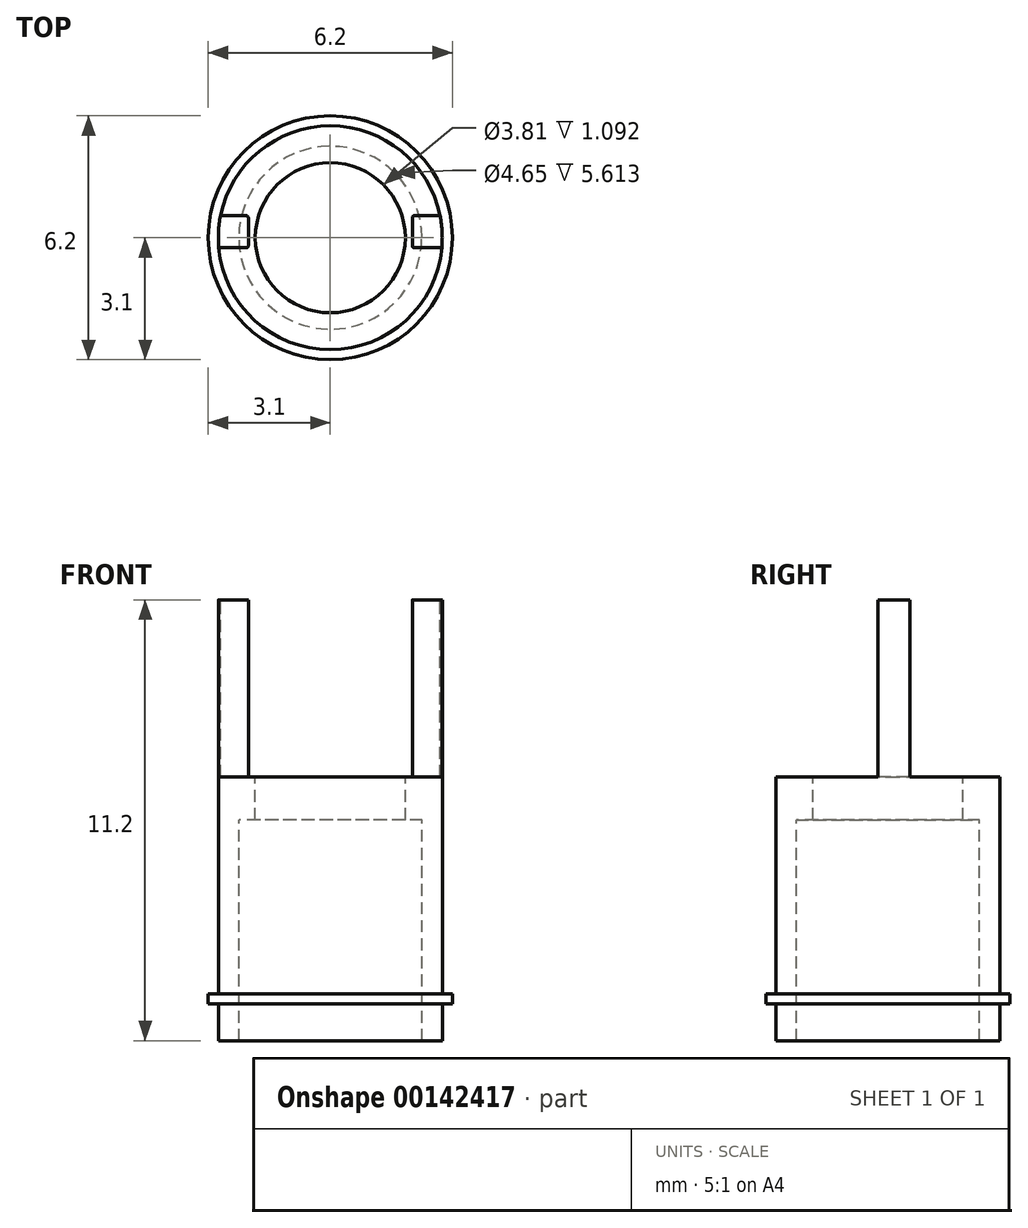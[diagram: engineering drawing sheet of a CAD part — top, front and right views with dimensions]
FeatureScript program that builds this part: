
annotation { "Feature Type Name" : "Feature", "Feature Type Description" : "" }
export const myFeature = defineFeature(function(context is Context, id is Id, definition is map)
    precondition{}
    {
        {
            var Q0;
            Q0=qCreatedBy(makeId("Right.planeOp"),FACE);
            var sketch = newSketch(context, id + "F0", { "sketchPlane" : qUnion([Q0])});
            skLineSegment(sketch, "E0", {"start": v(0, 0) * mm, "end": v(0, -11.2) * mm, "construction": true});
            skLineSegment(sketch, "E1", {"start": v(1.9, 0) * mm, "end": v(2.84, 0) * mm});
            skLineSegment(sketch, "E2", {"start": v(2.84, 0) * mm, "end": v(2.84, -10) * mm});
            skLineSegment(sketch, "E3", {"start": v(2.84, -10) * mm, "end": v(3.1, -10) * mm});
            skLineSegment(sketch, "E4", {"start": v(3.1, -10) * mm, "end": v(3.1, -10.26) * mm});
            skLineSegment(sketch, "E5", {"start": v(3.1, -10.26) * mm, "end": v(2.84, -10.26) * mm});
            skLineSegment(sketch, "E6", {"start": v(2.84, -10.26) * mm, "end": v(2.84, -11.2) * mm});
            skLineSegment(sketch, "E7", {"start": v(2.84, -11.2) * mm, "end": v(2.32, -11.2) * mm});
            skLineSegment(sketch, "E8", {"start": v(2.32, -11.2) * mm, "end": v(2.32, -5.59) * mm});
            skLineSegment(sketch, "E9", {"start": v(2.32, -5.59) * mm, "end": v(1.9, -5.59) * mm});
            skLineSegment(sketch, "E10", {"start": v(1.9, -5.59) * mm, "end": v(1.9, 0) * mm});
            skSolve(sketch);
        }
        {
            var Q0;
            Q0 = qSketchRegion(id + "F0", true);
            var Q1;
            Q1=sQuery(id+"F0.wireOp",EDGE,"E0");
            revolve(context, id + "F1", {"entities" : qUnion([Q0]), "axis" : qUnion([Q1]), "revolveType" : RevolveType.FULL});
        }
        {
            var Q0;
            Q0=makeQuery(id+"F1.opRevolve","SWEPT_FACE",FACE,{"disambiguationData":[OSD([sQuery(id+"F0.wireOp",EDGE,"E1")])]});
            var sketch = newSketch(context, id + "F2", { "sketchPlane" : qUnion([Q0])});
            skLineSegment(sketch, "E11", {"start": v(-3.61, 0) * mm, "end": v(4.59, 0) * mm, "construction": true});
            skLineSegment(sketch, "E12", {"start": v(0, 3.65) * mm, "end": v(0, -3.84) * mm, "construction": true});
            skLineSegment(sketch, "E13", {"start": v(-2.79, 0.56) * mm, "end": v(-2.08, 0.56) * mm});
            skLineSegment(sketch, "E14", {"start": v(-2.08, 0.56) * mm, "end": v(-2.08, -0.25) * mm});
            skLineSegment(sketch, "E15", {"start": v(-2.08, -0.25) * mm, "end": v(-2.83, -0.25) * mm});
            skLineSegment(sketch, "E16", {"start": v(2.79, 0.56) * mm, "end": v(2.08, 0.56) * mm});
            skLineSegment(sketch, "E17", {"start": v(2.08, 0.56) * mm, "end": v(2.08, -0.25) * mm});
            skLineSegment(sketch, "E18", {"start": v(2.08, -0.25) * mm, "end": v(2.83, -0.25) * mm});
            skSolve(sketch);
        }
        {
            var Q0;
            {var subQ5=sQuery(id+"F2.wireOp",EDGE,"E13");Q0=makeQuery(id+"F2.imprint","IMPRINT",FACE,{"disambiguationData":[TD([[makeQuery(id+"F2.imprint","IMPRINT",EDGE,{"derivedFrom":subQ5}),1.0]])]});}
            extrude(context, id + "F3", {"entities" : qUnion([Q0]), "operationType" : NewBodyOperationType.REMOVE, "oppositeDirection" : true, "depth" : 4.5 * mm});
        }
        {
            var Q0;
            Q0=makeQuery(id+"F3.boolean.opBoolean","COPY",EDGE,{"derivedFrom":makeQuery(id+"F3.opExtrude","SWEPT_EDGE",EDGE,{"disambiguationData":[OSD([sQuery(id+"F0.wireOp",EDGE,"E1"),sQuery(id+"F0.wireOp",EDGE,"E2"),sQuery(id+"F2.wireOp",EDGE,"E13")])]})});
            var Q1;
            Q1=makeQuery(id+"F3.boolean.opBoolean","COPY",EDGE,{"derivedFrom":makeQuery(id+"F3.opExtrude","SWEPT_EDGE",EDGE,{"disambiguationData":[OSD([sQuery(id+"F2.wireOp",EDGE,"E13"),sQuery(id+"F2.wireOp",EDGE,"E14")])]})});
            var Q2;
            Q2=makeQuery(id+"F3.boolean.opBoolean","COPY",EDGE,{"derivedFrom":makeQuery(id+"F3.opExtrude","SWEPT_EDGE",EDGE,{"disambiguationData":[OSD([sQuery(id+"F2.wireOp",EDGE,"E14"),sQuery(id+"F2.wireOp",EDGE,"E15")])]})});
            var Q3;
            Q3=makeQuery(id+"F3.boolean.opBoolean","COPY",EDGE,{"derivedFrom":makeQuery(id+"F3.opExtrude","SWEPT_EDGE",EDGE,{"disambiguationData":[OSD([sQuery(id+"F0.wireOp",EDGE,"E1"),sQuery(id+"F0.wireOp",EDGE,"E2"),sQuery(id+"F2.wireOp",EDGE,"E15")])]})});
            var Q4;
            Q4=makeQuery(id+"F3.boolean.opBoolean","COPY",EDGE,{"derivedFrom":makeQuery(id+"F3.opExtrude","SWEPT_EDGE",EDGE,{"disambiguationData":[OSD([sQuery(id+"F2.wireOp",EDGE,"E17"),sQuery(id+"F2.wireOp",EDGE,"E18")])]})});
            var Q5;
            Q5=makeQuery(id+"F3.boolean.opBoolean","COPY",EDGE,{"derivedFrom":makeQuery(id+"F3.opExtrude","SWEPT_EDGE",EDGE,{"disambiguationData":[OSD([sQuery(id+"F0.wireOp",EDGE,"E1"),sQuery(id+"F0.wireOp",EDGE,"E2"),sQuery(id+"F2.wireOp",EDGE,"E18")])]})});
            var Q6;
            Q6=makeQuery(id+"F3.boolean.opBoolean","COPY",EDGE,{"derivedFrom":makeQuery(id+"F3.opExtrude","SWEPT_EDGE",EDGE,{"disambiguationData":[OSD([sQuery(id+"F0.wireOp",EDGE,"E1"),sQuery(id+"F0.wireOp",EDGE,"E2"),sQuery(id+"F2.wireOp",EDGE,"E16")])]})});
            var Q7;
            Q7=makeQuery(id+"F3.boolean.opBoolean","COPY",EDGE,{"derivedFrom":makeQuery(id+"F3.opExtrude","SWEPT_EDGE",EDGE,{"disambiguationData":[OSD([sQuery(id+"F2.wireOp",EDGE,"E16"),sQuery(id+"F2.wireOp",EDGE,"E17")])]})});
            fillet(context, id + "F4", {"entities" : qUnion([Q0, Q1, Q2, Q3, Q4, Q5, Q6, Q7]), "radius" : 0.05 * mm, "tangentPropagation" : true, "allowEdgeOverflow" : false});
        }
    });
